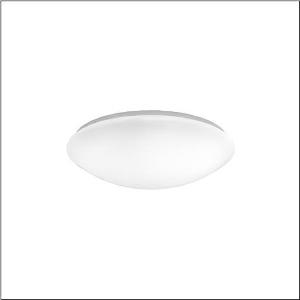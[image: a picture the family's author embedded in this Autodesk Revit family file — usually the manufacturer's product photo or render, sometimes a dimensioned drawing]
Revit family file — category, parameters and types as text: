
# Revit family: round_31_b_5pja110001a
name_source: partatom
category: Lighting Fixtures
units: mm (PartAtom-declared; Revit-internal decimal feet)

## family parameters
Cut with Voids When Loaded = No
Host = Face
Light Source = No
Part Type = Normal
Room Calculation Point = No
Round Connector Dimension = Use Diameter
Shared = No

## types (1)
- Round 31 B (1 x LED, 2520 lm, 21 W, 3000K)
    Apparent Load = 21 VA
    CIE Flux Codes = 42 71 89 88 100
    Color Rendering = 80
    Color Temperature = 3000K
    Default Elevation = 1800 mm
    Description = Round 31 B, wall and ceiling luminaire, primary optical cover: enclosure, of PMMA, light emission: direct distribution, primary light characteristic: symmetric, installation type: surface-mounted, LED, rated luminous flux: 2.520lm, luminous efficacy: 120lm/W, light colour: 830, colour temperature: 3000K, with terminal, 3-pole, max. 2.5mm², mains connection: 230V, AC, 50/60Hz, rated input power: 21W, luminaire housing, round, of steel, white, diameter: 360mm, height: 95mm, protection rating (complete): IP40, insulation class (complete): insulation class I (protective earthing), certification: CE, impact resistance: IK02, permissible operating ambient temperature: -20..+25°C, packaging unit: 1 piece
    Height = 95 mm
    Lamp = 1 x LED
    Lamp Light Flux = 2520 lm
    Lamp Power = 21 W
    Lamp count = 1
    Length = 360 mm
    Luminous efficacy = 120 lm/W
    Manufacturer = Siteco
    ModVariant = No
    Model = 5PJA110001A
    Mounting Place = Ceiling
    Mounting Type = Surface mounted
    Number of Poles = 1
    OnlyDefault = Yes
    Power Factor = 1
    Product Name = Round 31 B
    Product group = wall and ceiling luminaire
    ProductGroupID = 301
    Protection Class = Protection class I
    Protection Degree = IP 40
    RLX_Detail_Level = 1
    RLX_Emergency_Light_Flux = 0 lm
    RLX_Emergency_Type = 0
    RLX_Emergency_Type_DB = No
    RlxData = <blob elided: 10985 chars, md5=00631781>
    Socket = socket
    Standby Power = 0 W
    System Light Flux = 2520 lm
    System Power = 21 W
    Type Comments = Product without accessories
    Type Image = l_1258315.jpg
    URL = http://relux.com
    VarID = ---
    Voltage = 0 V
    Weight = 0.00 kg
    Width = 0 mm  [stored 0 ft]

note: [stored X ft] marks values corroborated as IEEE doubles in the binary element streams (Revit-internal decimal feet)

## geometry (parser evidence)
native form markers: Sweep x11
no freeform markers — native parametric forms only
